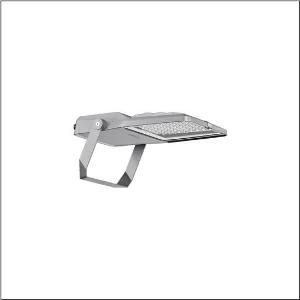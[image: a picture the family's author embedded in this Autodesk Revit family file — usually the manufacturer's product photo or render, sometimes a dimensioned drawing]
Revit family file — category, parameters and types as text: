
# Revit family: floodlight_fl_21_iq_mini___pl43_5xa7771c4a1a_6230
name_source: partatom
category: Lighting Fixtures
units: mm (PartAtom-declared; Revit-internal decimal feet)

## family parameters
Cut with Voids When Loaded = No
Host = Face
Light Source = No
Part Type = Normal
Room Calculation Point = No
Round Connector Dimension = Use Diameter
Shared = No

## types (1)
- --- (1 x LED, 13050 lm, 87.2 W, 4000K)
    Apparent Load = 87 VA
    CIE Flux Codes = 27 78 99 100 100
    Color Rendering = 70
    Color Temperature = 4000K
    Default Elevation = 1800 mm
    Description = Floodlight FL 21 iQ mini, floodlight, primary light control with lens, of PMMA, primary optical cover: protective disc, of toughened safety glass, transparent, light distribution: PL43, light emission: direct distribution, installation type: surface-mounted, lamps: LED, High Power LED, rated values: 13.050lm | 87,2W | 149,7lm/W (begin service life); end service life: 13.050lm | 92,1W; at 50% lumin. flux: 6.525lm | 40,2W | 162,3lm/W, colour temperature: 4000K, colour rendering: CRI > 70, light colour: 740, light setting 1 begin service life: 100% | 13.050lm | 87,2W | 149,7lm/W | 4.000K, light setting 1 end service life: 92,1W, further light settings possible, control: Auto-Match, Temp-Guard, Lumen-Switch, Night-Set, Smart-Wire, Light-Fading, Desk-Remote (wireless, voltage-free reading and setting of iQ features in the workshop via application-optimized NFC function/RFID function), optimised constant luminous flux control (CLO 2.0), pre-setting: linear dimming characteristic, with terminal, 6-pole, mains connection: 220..240V, AC, 50/60Hz, luminaire housing, of diecast aluminium, powder-coated, SITECO metallic grey (DB 702S), corrosivity category C5 mid according to DIN EN ISO 12944suitable for swimming poolschlorine-resistant, sealing non-destructively replaceable, mounting bracket, of steel, galvanised, powder-coated, SITECO metallic grey (DB 702S), protection rating (complete): IP66, insulation class (complete): insulation class II (safety insulation), certification: CE, ENEC, VDE, protection symbol: D, impact resistance: IK08, permissible operating ambient temperature: -40..+40°C, permissible operating ambient temperature for outdoor applications: -40..+50°C, standard: DIN EN 12944, LABS conformity tested according to VDMA 24364:2018-05, packaging unit: 1 piece

Light Distribution: PL43
    Height = 70 mm
    Lamp = 1 x LED
    Lamp Light Flux = 13050 lm
    Lamp Power = 87.2 W
    Lamp count = 1
    Length = 485 mm
    Luminous efficacy = 150 lm/W
    Manufacturer = Siteco
    ModVariant = No
    Model = 5XA7771C4A1A
    Mounting Place = Pole
    Mounting Type = Pole annexe
    Number of Poles = 1
    OnlyDefault = Yes
    Power Factor = 1
    Product Name = Floodlight FL 21 iQ mini | PL43
    Product group = floodlight | pylon annexe
    ProductGroupID = 6201
    Protection Class = Protection class II
    Protection Degree = IP 66
    RLX_Detail_Level = 1
    RLX_Emergency_Light_Flux = 0 lm
    RLX_Emergency_Type = 0
    RLX_Emergency_Type_DB = No
    RlxData = <blob elided: 96513 chars, md5=bc5584cf>
    Socket = socket
    Standby Power = 0 W
    System Light Flux = 13050 lm
    System Power = 87 W
    Type Comments = factory setting: luminous flux: 100 % | dim-lin: 254 | 456 mA
    Type Image = l_1006845.jpg
    URL = http://relux.com
    VarID = @adj_162959
    Voltage = 0 V
    Weight = 0.00 kg
    Width = 337 mm

## geometry (parser evidence)
native form markers: Blend x4, Sweep x10
no freeform markers — native parametric forms only
